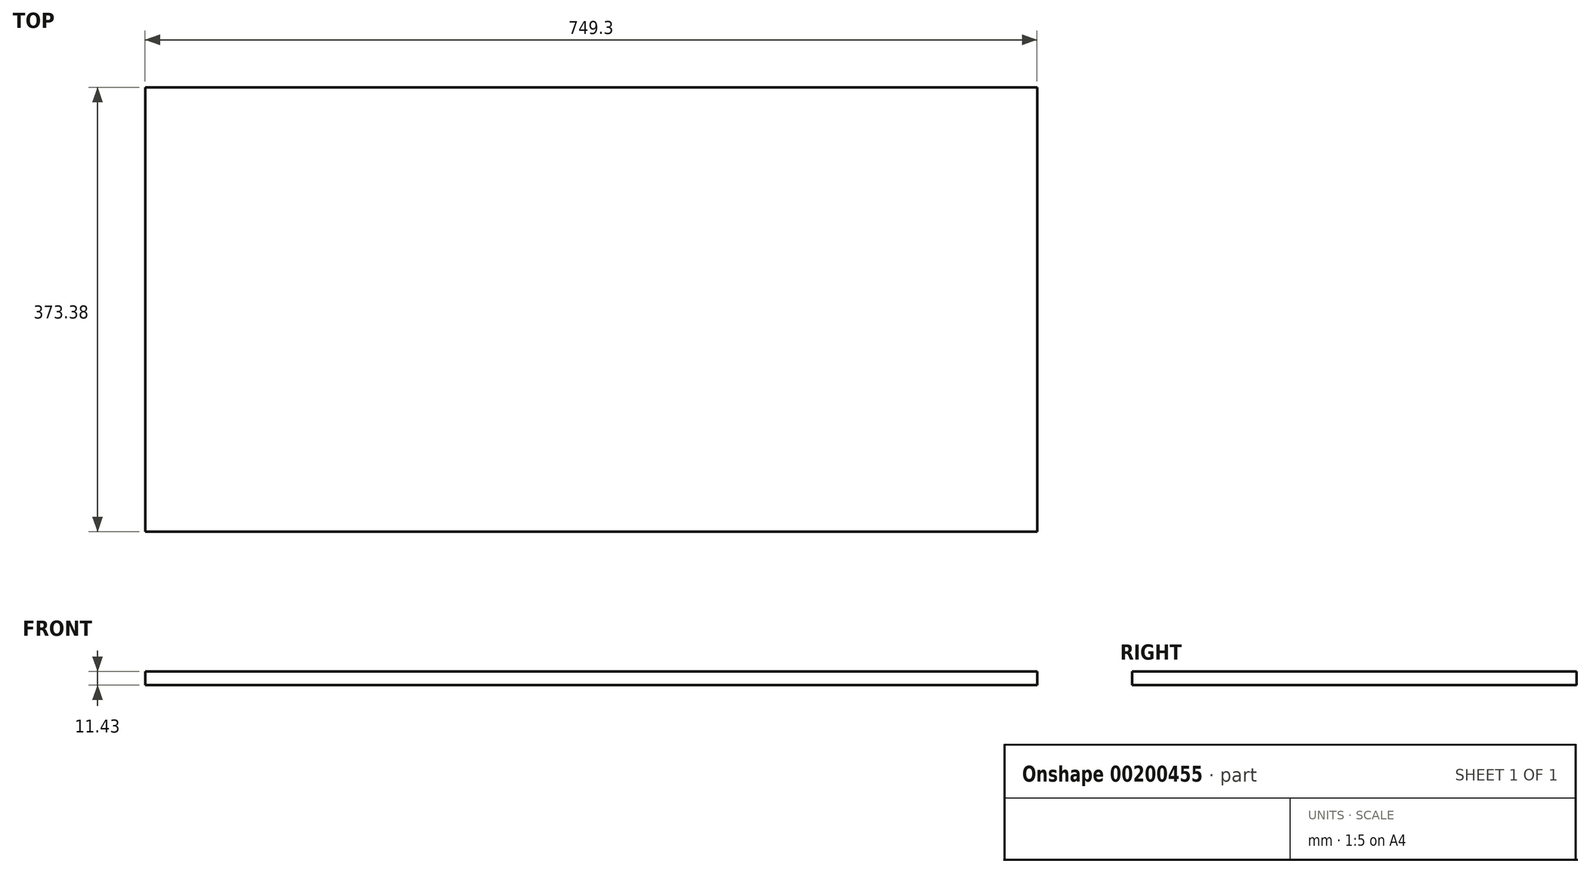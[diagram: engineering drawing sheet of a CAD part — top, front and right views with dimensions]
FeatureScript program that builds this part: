
annotation { "Feature Type Name" : "Feature", "Feature Type Description" : "" }
export const myFeature = defineFeature(function(context is Context, id is Id, definition is map)
    precondition{}
    {
        {
            var Q0;
            Q0=qCreatedBy(makeId("Top.planeOp"),FACE);
            var sketch = newSketch(context, id + "F0", { "sketchPlane" : qUnion([Q0])});
            skLineSegment(sketch, "E0.bottom", {"start": v(-54.23, 359.01) * mm, "end": v(695.07, 359.01) * mm});
            skLineSegment(sketch, "E0.top", {"start": v(-54.23, -14.37) * mm, "end": v(695.07, -14.37) * mm});
            skLineSegment(sketch, "E0.left", {"start": v(-54.23, 359.01) * mm, "end": v(-54.23, -14.37) * mm});
            skLineSegment(sketch, "E0.right", {"start": v(695.07, 359.01) * mm, "end": v(695.07, -14.37) * mm});
            skSolve(sketch);
        }
        {
            var Q0;
            Q0=makeQuery(id+"F0.imprint","IMPRINT",FACE,{"disambiguationData":[TD([[makeQuery(id+"F0.imprint","IMPRINT",EDGE,{"derivedFrom":sQuery(id+"F0.wireOp",EDGE,"E0.bottom")}),-1.0]])]});
            extrude(context, id + "F1", {"entities" : qUnion([Q0]), "depth" : 11.43 * mm});
        }
    });
